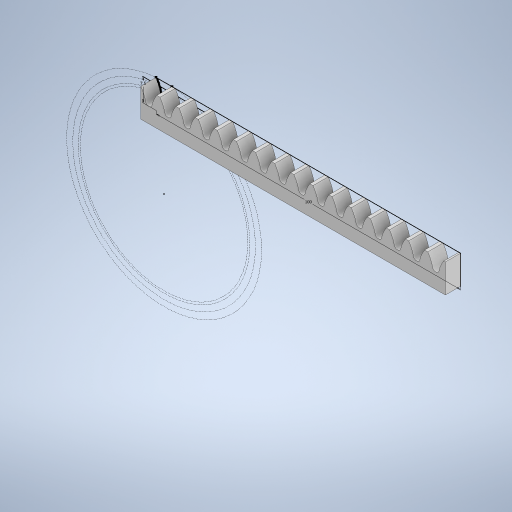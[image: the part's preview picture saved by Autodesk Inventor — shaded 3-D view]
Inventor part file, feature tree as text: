
AUTODESK INVENTOR PART (.ipt)
format: ipt  version: 2023 (Build 270158000, 158)  size: 335,872 bytes
history: native  units: mm
features: extrude x2, pattern_linear x1
ambient origin geometry x8: Origin, YZ Plane, XZ Plane, XY Plane, X Axis, Y Axis, Z Axis, Center Point
bodies: Body1 (feature_tree)
feature tree (3):
  extrude  "Extrusion2"  Depth=100.0mm
  extrude  "Extrusion3"  Depth=5.0mm TaperAngle=0.0deg
  pattern_linear  "Rectangular Pattern1"  Spacing1=0.0mm  [1 undecoded]
note: 1 required parameter value undecoded (feature->parameter linkage not recoverable at this tier; creation-order binding heuristic only, values carry confidence <= 0.55)
